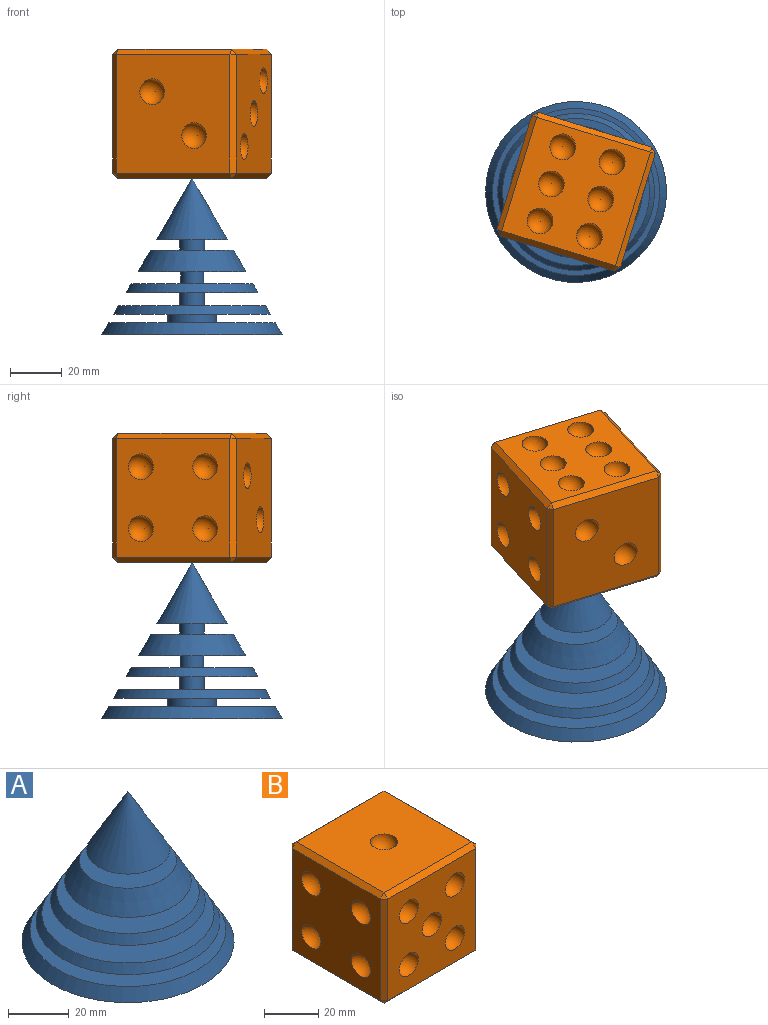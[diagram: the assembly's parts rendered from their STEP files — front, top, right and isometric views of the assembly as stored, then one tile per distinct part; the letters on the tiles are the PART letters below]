
ASSEMBLY  parts=2 mates=1
PART A: 18 faces, bbox 70x70x60.6 mm
  f0: cylinder r=4.48mm len=8.96mm, axis (0,0,-1), area 129.7mm2, adj f1,f17
  f1: plane 47.09x47.09mm, normal (0,0,1), area 1678.3mm2, adj f0,f2
  f2: cone r=23.54mm half-angle=30deg, axis (0,0,-1), area 609.6mm2, adj f1,f3
  f3: plane 51.04x51.04mm, normal (0,0,-1), area 1976.5mm2, adj f2,f4
  f4: cylinder r=4.71mm len=9.42mm, axis (0,0,-1), area 149.5mm2, adj f3,f5
  f5: plane 56.87x56.87mm, normal (0,0,1), area 2470.9mm2, adj f4,f6
  f6: cone r=28.44mm half-angle=30deg, axis (0,0,-1), area 709mm2, adj f5,f7
  f7: plane 60.71x60.71mm, normal (0,0,-1), area 2620.8mm2, adj f6,f8
  f8: cylinder r=9.34mm len=18.69mm, axis (0,0,-1), area 200.7mm2, adj f7,f9
  f9: plane 64.66x64.66mm, normal (0,0,1), area 3009.5mm2, adj f8,f10
  f10: cone r=35mm half-angle=30deg, axis (0,0,-1), area 1129.4mm2, adj f9,f11
  f11: plane 70x70mm, normal (0,0,-1), area 3848.5mm2, adj f10
  f12: cone r=13.69mm half-angle=30deg, axis (0,0,-1), area 1178.1mm2, adj f13
  f13: plane 27.39x27.39mm, normal (0,0,-1), area 515.9mm2, adj f12,f14
  f14: cylinder r=4.83mm len=9.65mm, axis (0,0,-1), area 123.4mm2, adj f13,f15
  f15: plane 32.08x32.08mm, normal (0,0,1), area 735.2mm2, adj f14,f16
  f16: cone r=20.88mm half-angle=30deg, axis (0,0,-1), area 1122.9mm2, adj f15,f17
  f17: plane 41.76x41.76mm, normal (0,0,-1), area 1306.9mm2, adj f0,f16
PART B: 47 faces, bbox 50x50x50 mm
  f0: plane 46x46mm, normal (-1,0,0), area 1801.8mm2, adj f23,f24,f25,f26,f33,f34,f42,f43
  f1: plane 46x46mm, normal (0,1,0), area 1958.9mm2, adj f21,f22,f35,f40,f43,f46
  f2: plane 46x46mm, normal (0,0,-1), area 1644.8mm2, adj f9,f10,f11,f12,f13,f14,f27,f30
  f3: plane 46x46mm, normal (0,-1,0), area 1723.3mm2, adj f16,f17,f18,f19,f20,f27,f31,f32
  f4: plane 46x46mm, normal (1,0,0), area 1880.4mm2, adj f6,f7,f8,f30,f31,f40,f41
  f5: plane 46x46mm, normal (0,0,1), area 2037.5mm2, adj f15,f32,f41,f42,f46
  f6: sphere r=5mm, area 157.1mm2, adj f4
  f7: sphere r=5mm, area 157.1mm2, adj f4
  f8: sphere r=5mm, area 157.1mm2, adj f4
  f9: sphere r=5mm, area 157.1mm2, adj f2
  f10: sphere r=5mm, area 157.1mm2, adj f2
  f11: sphere r=5mm, area 157.1mm2, adj f2
  f12: sphere r=5mm, area 157.1mm2, adj f2
  f13: sphere r=5mm, area 157.1mm2, adj f2
  f14: sphere r=5mm, area 157.1mm2, adj f2
  f15: sphere r=5mm, area 157.1mm2, adj f5
  f16: sphere r=5mm, area 157.1mm2, adj f3
  f17: sphere r=5mm, area 157.1mm2, adj f3
  f18: sphere r=5mm, area 157.1mm2, adj f3
  f19: sphere r=5mm, area 157.1mm2, adj f3
  f20: sphere r=5mm, area 157.1mm2, adj f3
  f21: sphere r=5mm, area 157.1mm2, adj f1
  f22: sphere r=5mm, area 157.1mm2, adj f1
  f23: sphere r=5mm, area 157.1mm2, adj f0
  f24: sphere r=5mm, area 157.1mm2, adj f0
  f25: sphere r=5mm, area 157.1mm2, adj f0
  f26: sphere r=5mm, area 157.1mm2, adj f0
  f27: plane 46x2mm, normal (0,-0.71,-0.71), area 130.1mm2, adj f2,f3,f28,f29
  f28: plane 2x2mm, normal (0.58,-0.58,-0.58), area 3.5mm2, adj f27,f30,f31
  f29: plane 2x2mm, normal (-0.58,-0.58,-0.58), area 3.5mm2, adj f27,f33,f34
  f30: plane 46x2mm, normal (0.71,0,-0.71), area 130.1mm2, adj f2,f4,f28,f36
  f31: plane 46x2mm, normal (0.71,-0.71,0), area 130.1mm2, adj f3,f4,f28,f37
  f32: plane 46x2mm, normal (0,-0.71,0.71), area 130.1mm2, adj f3,f5,f37,f38
  f33: plane 46x2mm, normal (-0.71,-0.71,0), area 130.1mm2, adj f0,f3,f29,f38
  f34: plane 46x2mm, normal (-0.71,0,-0.71), area 130.1mm2, adj f0,f2,f29,f39
  f35: plane 46x2mm, normal (0,0.71,-0.71), area 130.1mm2, adj f1,f2,f36,f39
  f36: plane 2x2mm, normal (0.58,0.58,-0.58), area 3.5mm2, adj f30,f35,f40
  f37: plane 2x2mm, normal (0.58,-0.58,0.58), area 3.5mm2, adj f31,f32,f41
  f38: plane 2x2mm, normal (-0.58,-0.58,0.58), area 3.5mm2, adj f32,f33,f42
  f39: plane 2x2mm, normal (-0.58,0.58,-0.58), area 3.5mm2, adj f34,f35,f43
  f40: plane 46x2mm, normal (0.71,0.71,0), area 130.1mm2, adj f1,f4,f36,f44
  f41: plane 46x2mm, normal (0.71,0,0.71), area 130.1mm2, adj f4,f5,f37,f44
  f42: plane 46x2mm, normal (-0.71,0,0.71), area 130.1mm2, adj f0,f5,f38,f45
  f43: plane 46x2mm, normal (-0.71,0.71,0), area 130.1mm2, adj f0,f1,f39,f45
  f44: plane 2x2mm, normal (0.58,0.58,0.58), area 3.5mm2, adj f40,f41,f46
  f45: plane 2x2mm, normal (-0.58,0.58,0.58), area 3.5mm2, adj f42,f43,f46
  f46: plane 46x2mm, normal (0,0.71,0.71), area 130.1mm2, adj f1,f5,f44,f45
PLACE A at identity fixed
PLACE B rot(axis=(0.99,-0.15,0),180deg) t=(0,0,85.62)mm
MATE cylindrical B.f5 <-> A.f10  axis (0,0,-1) through (0,0,60.62)mm
